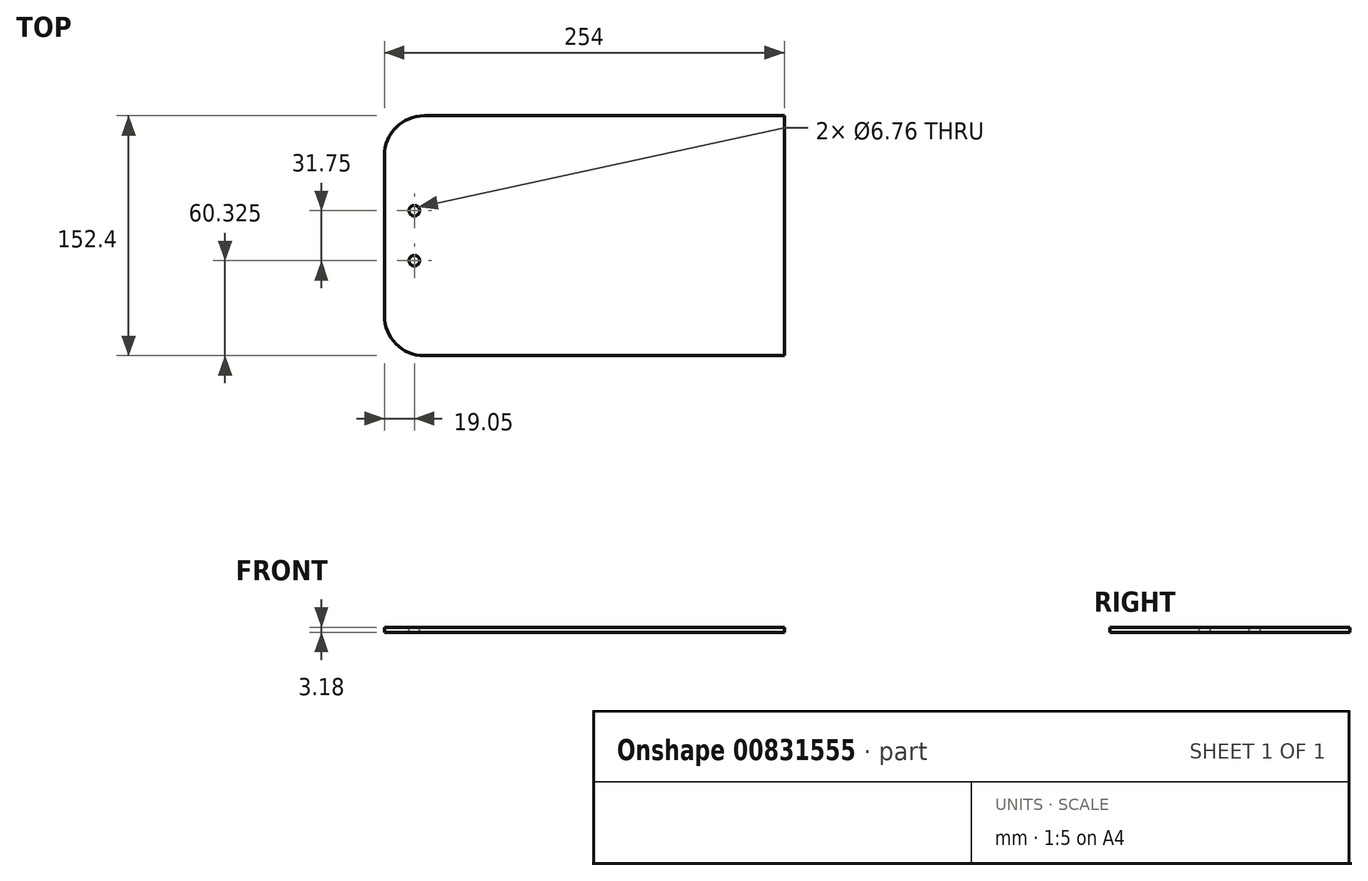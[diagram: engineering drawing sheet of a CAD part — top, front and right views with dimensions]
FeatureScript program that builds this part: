
annotation { "Feature Type Name" : "Feature", "Feature Type Description" : "" }
export const myFeature = defineFeature(function(context is Context, id is Id, definition is map)
    precondition{}
    {
        {
            var Q0;
            Q0=qCreatedBy(makeId("Top.planeOp"),FACE);
            var sketch = newSketch(context, id + "F0", { "sketchPlane" : qUnion([Q0])});
            skLineSegment(sketch, "E0.bottom", {"start": v(-101.6, 76.2) * mm, "end": v(127, 76.2) * mm});
            skLineSegment(sketch, "E0.top", {"start": v(-101.6, -76.2) * mm, "end": v(127, -76.2) * mm});
            skLineSegment(sketch, "E0.left", {"start": v(-127, 50.8) * mm, "end": v(-127, -50.8) * mm});
            skLineSegment(sketch, "E0.right", {"start": v(127, 76.2) * mm, "end": v(127, -76.2) * mm});
            skLineSegment(sketch, "E1", {"start": v(0, 76.2) * mm, "end": v(0, 0) * mm, "construction": true});
            skLineSegment(sketch, "E2", {"start": v(0, 0) * mm, "end": v(0, -76.2) * mm, "construction": true});
            skPoint(sketch, "E3.visualSharp", {"position": v(-127, 76.2) * mm});
            skArc(sketch, "E3.filletArc", {"start": v(-101.6, 76.2) * mm, "mid": v(-119.56, 68.76) * mm, "end": v(-127, 50.8) * mm});
            skPoint(sketch, "E4.visualSharp", {"position": v(-127, -76.2) * mm});
            skArc(sketch, "E4.filletArc", {"start": v(-127, -50.8) * mm, "mid": v(-119.56, -68.76) * mm, "end": v(-101.6, -76.2) * mm});
            skSolve(sketch);
        }
        {
            var Q0;
            Q0=makeQuery(id+"F0.imprint","IMPRINT",FACE,{"disambiguationData":[TD([[makeQuery(id+"F0.imprint","IMPRINT",EDGE,{"derivedFrom":sQuery(id+"F0.wireOp",EDGE,"E0.bottom")}),-1.0]])]});
            extrude(context, id + "F1", {"entities" : qUnion([Q0]), "depth" : 3.17 * mm, "offsetDistance" : 25.4 * mm});
        }
        {
            var Q0;
            Q0=makeQuery(id+"F1.opExtrude","CAP_FACE",FACE,{"disambiguationData":[OSD([sQuery(id+"F0.wireOp",EDGE,"E0.bottom"),sQuery(id+"F0.wireOp",EDGE,"E0.top"),sQuery(id+"F0.wireOp",EDGE,"E0.left"),sQuery(id+"F0.wireOp",EDGE,"E0.right")])],"isStart":false});
            var sketch = newSketch(context, id + "F2", { "sketchPlane" : qUnion([Q0])});
            skPoint(sketch, "E5", {"position": v(-107.95, 15.88) * mm});
            skPoint(sketch, "E6", {"position": v(-107.95, -15.88) * mm});
            skLineSegment(sketch, "E7", {"start": v(-107.95, -15.88) * mm, "end": v(-107.95, 15.88) * mm, "construction": true});
            skLineSegment(sketch, "E8", {"start": v(0, 0) * mm, "end": v(-107.95, 0) * mm, "construction": true});
            skSolve(sketch);
        }
        {
            var Q0;
            Q0=sQuery(id+"F2.wireOp",VERTEX,"E7.end");
            var Q1;
            Q1=sQuery(id+"F2.wireOp",VERTEX,"E6");
            var Q2;
            Q2=makeQuery(id+"F1.opExtrude","SWEPT_BODY",BODY,{"disambiguationData":[OSD([sQuery(id+"F0.wireOp",EDGE,"E0.bottom"),sQuery(id+"F0.wireOp",EDGE,"E0.top"),sQuery(id+"F0.wireOp",EDGE,"E0.left"),sQuery(id+"F0.wireOp",EDGE,"E0.right")])]});
            hole(context, id + "F3", {"style" : HoleStyle.SIMPLE, "endStyle" : HoleEndStyle.THROUGH, "standardTappedOrClearance" : lookupTablePath({ "fit" : "Normal (ASME)", "standard" : "ANSI", "size" : "1/4", "type" : "Clearance" }), "standardBlindInLast" : lookupTablePath({ "fit" : "Free", "standard" : "ANSI", "size" : "1/4", "type" : "Clearance" }), "holeDiameter" : 6.76 * mm, "majorDiameter" : 6.35 * mm, "isTappedThrough" : true, "tappedDepth" : 12.7 * mm, "tapClearance" : 3, "locations" : qUnion([Q0, Q1]), "scope" : qUnion([Q2])});
        }
    });
